# Revit family: Auto-Door_Sliding_BiPart_Wall_Tormax_TX9500SM
name_source: partatom
category: Doors
units: mm (PartAtom-declared; Revit-internal decimal feet)

## family parameters
Always vertical = Yes
Cut with Voids When Loaded = No
Host = Wall
OmniClass Number = 23.30.10.17.11
OmniClass Title = Sliding Doors
Room Calculation Point = No
Shared = No

## types (2) — shared parameters
Analytic Construction = <None>
Assembly Code = B2030110
Available Options = [Standard Weatherstripping][Electric Lock][Battery Backup][Door Position Monitoring][I/O Module][Key Switch]
Construction Details = http://www.arcat.com
Define Thermal Properties by = Schematic Type
Fire Rating = as Specified
Frame Thickness = 4 1/2"
Glazing Thickness_Fixed Panel = 1 3/4"
Glazing Thickness_Sliding Panel = 1/2"
Green Building-LEED = http://www.arcat.com
Has Partial Breakout Capability = Yes
Height = 95"
Keynote = 08463
Manufacturer = TORMAX USA Inc.
Manufacturer Fax = 210-494-5930
Manufacturer Website = http://www.tormaxusa.com
Max Height = 0"
Max Width = 0"
Miami Dade Conformance = Does Not Apply
Opening Height = 83 5/8"
Operating Temperature Range = Ambient -30F to 130F
Panel Thickness = 1 3/4"
Product Data = http://www.arcat.com
Sales Information = http://www.tormaxusa.com
Send Message = http://www.arcat.com
Specification = http://www.arcat.com
Standards Conformance = ANSI A156.10  ;  NFPA 101  ;  UL325  ;  C-UL
Thickness = 1 3/4"
URL = http://www.tormaxusa.com
Wall Closure = By host
Water Penetration = as Specified
zero-valued in all types: Expected Lifespan (Years), Maintenance Schedule (Months), Warranty Duration (Years)

## per-type parameters (varying)
| type | Description | HD Drive | Model | headerdepth |
| HD OXXO | Tormax HD Automatic Sliding BiPart Door - All Glass TX9500HDSM as Specified | Yes | TX9500HDSM as Specified | 9 1/2" |
| OXXO | Tormax Automatic Sliding BiPart Door - All Glass TX9500SM as Specified | No | TX9500SM as Specified | 8" |

## geometry (parser evidence)
native form markers: Sweep x8
no freeform markers — native parametric forms only
